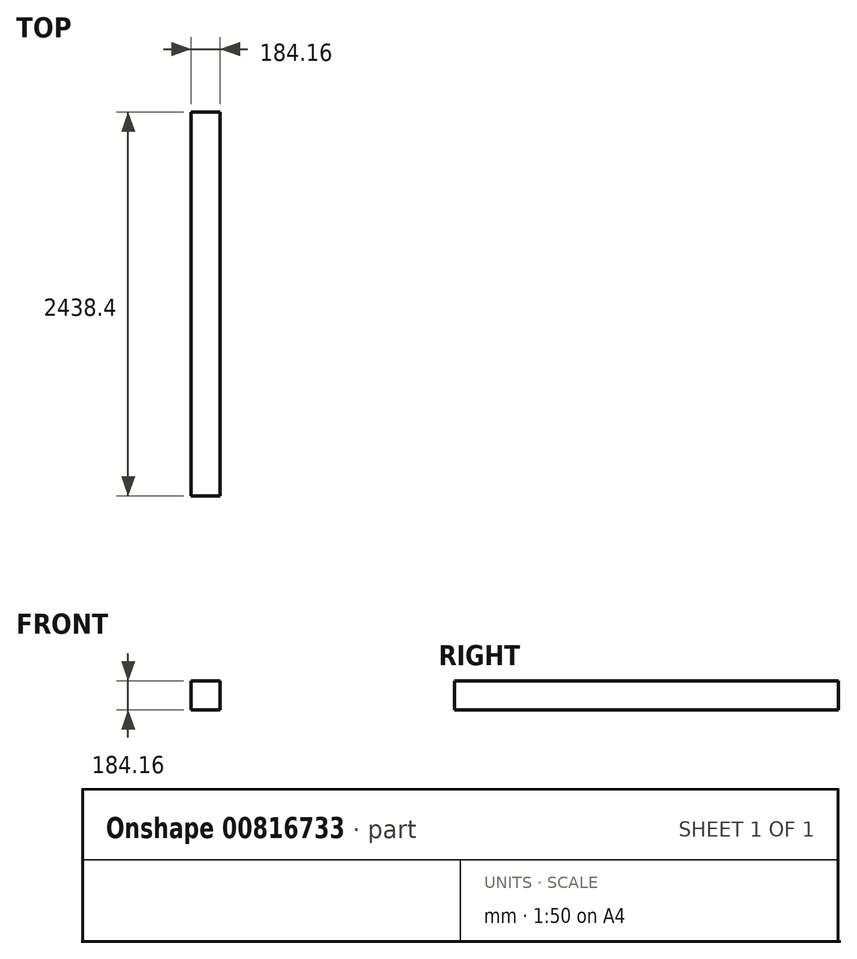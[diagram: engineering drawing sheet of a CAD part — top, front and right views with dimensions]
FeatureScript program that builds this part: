
annotation { "Feature Type Name" : "Feature", "Feature Type Description" : "" }
export const myFeature = defineFeature(function(context is Context, id is Id, definition is map)
    precondition{}
    {
        {
            var Q0;
            Q0=qCreatedBy(makeId("Front.planeOp"),FACE);
            var sketch = newSketch(context, id + "F0", { "sketchPlane" : qUnion([Q0])});
            skLineSegment(sketch, "E0.bottom", {"start": v(92.08, -92.08) * mm, "end": v(-92.08, -92.08) * mm});
            skLineSegment(sketch, "E0.top", {"start": v(92.08, 92.08) * mm, "end": v(-92.08, 92.08) * mm});
            skLineSegment(sketch, "E0.left", {"start": v(92.08, -92.07) * mm, "end": v(92.08, 92.08) * mm});
            skLineSegment(sketch, "E0.right", {"start": v(-92.08, -92.08) * mm, "end": v(-92.08, 92.08) * mm});
            skPoint(sketch, "E0.middle", {"position": v(0, 0) * mm});
            skSolve(sketch);
        }
        {
            var Q0;
            Q0=makeQuery(id+"F0.imprint","IMPRINT",FACE,{"disambiguationData":[TD([[makeQuery(id+"F0.imprint","IMPRINT",EDGE,{"derivedFrom":sQuery(id+"F0.wireOp",EDGE,"E0.bottom")}),-1.0]])]});
            extrude(context, id + "F1", {"entities" : qUnion([Q0]), "endBound" : BoundingType.SYMMETRIC, "depth" : 2438.4 * mm, "offsetDistance" : 25.4 * mm});
        }
    });
